FCSTD DOCUMENT
Label: PCB Dimensions
objects: Sketcher::SketchObject×1
note: 1 computed .brp shape members not serialized (recipe doc carries the construction recipe); baked Part::Feature solids carry a one-line shape summary decoded from their .brp

FEATURE [Sketcher::SketchObject] Sketch
  sketch-geometry (6):
    g0: LineSegment StartX=-44.45 StartY=142.24 StartZ=0 EndX=44.45 EndY=142.24 EndZ=0
    g1: LineSegment StartX=44.45 StartY=142.24 StartZ=0 EndX=177.8 EndY=-53.34 EndZ=0
    g2: LineSegment StartX=177.8 StartY=-53.34 StartZ=0 EndX=177.8 EndY=-142.24 EndZ=0
    g3: LineSegment StartX=177.8 StartY=-142.24 StartZ=0 EndX=-177.8 EndY=-142.24 EndZ=0
    g4: LineSegment StartX=-177.8 StartY=-142.24 StartZ=0 EndX=-177.8 EndY=-53.34 EndZ=0
    g5: LineSegment StartX=-177.8 StartY=-53.34 StartZ=0 EndX=-44.45 EndY=142.24 EndZ=0
  constraints (18):
    c: Horizontal(g0)
    c: Coincident(g0,g1)
    c: Coincident(g1,g2)
    c: Vertical(g2)
    c: Coincident(g2,g3)
    c: Coincident(g3,g4)
    c: Coincident(g4,g5)
    c: Coincident(g5,g0)
    c: Parallel(g0,g3)
    c: Parallel(g4,g2)
    c: DistanceY(g0,g3) = -284.48
    c: DistanceX(g2,g3) = -355.6
    c: DistanceY(g4,g3) = -88.9
    c: DistanceX(g0,g0) = 88.9
    c: DistanceX(g4,g0) = 133.35
    c: DistanceX(g-1,g2) = 177.8
    c: DistanceY(g-1,g4) = -53.34
    c: DistanceY(g0,g1) = -195.58
